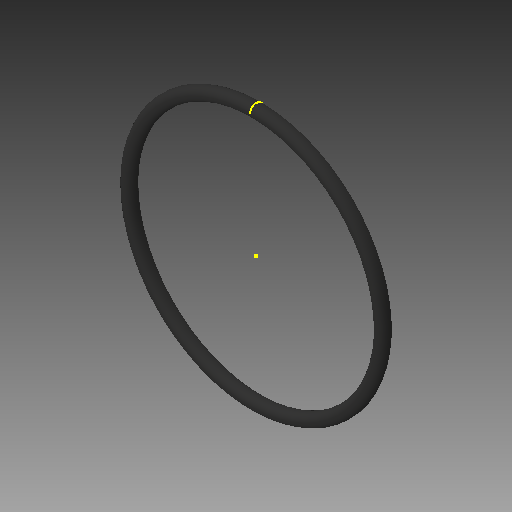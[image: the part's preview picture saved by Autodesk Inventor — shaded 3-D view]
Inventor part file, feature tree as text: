
AUTODESK INVENTOR PART (.ipt)
format: ipt  version: 2018 (Build 220112000, 112)  size: 128,000 bytes
history: native  units: in
note: dims shown in document units (in); Inventor stores cm internally (conversion verified against a paired STEP export)
features: sketch x1, revolve x1
ambient origin geometry x8: Origin, YZ Plane, XZ Plane, XY Plane, X Axis, Y Axis, Z Axis, Center Point
bodies: Solid1 (feature_tree)
feature tree (2):
  sketch  "Sketch1"
  revolve  "Revolve1"  [1 undecoded]
note: 1 required parameter value undecoded (feature->parameter linkage not recoverable at this tier; creation-order binding heuristic only, values carry confidence <= 0.55)
